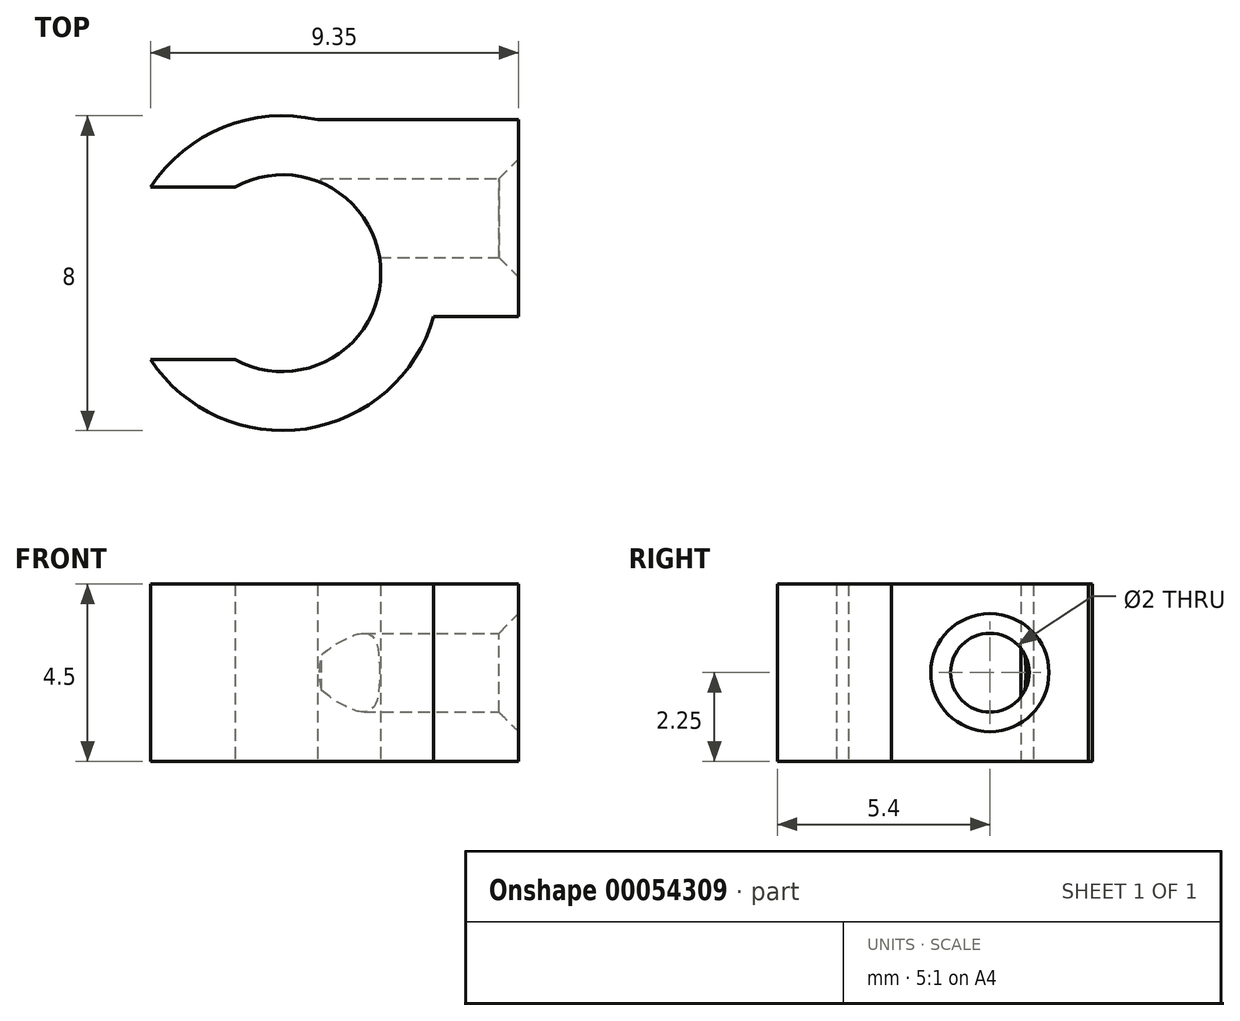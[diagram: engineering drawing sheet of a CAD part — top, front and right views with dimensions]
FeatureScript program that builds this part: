
annotation { "Feature Type Name" : "Feature", "Feature Type Description" : "" }
export const myFeature = defineFeature(function(context is Context, id is Id, definition is map)
    precondition{}
    {
        {
            var Q0;
            Q0=qCreatedBy(makeId("Top.planeOp"),FACE);
            var sketch = newSketch(context, id + "F0", { "sketchPlane" : qUnion([Q0])});
            skArc(sketch, "E0", {"start": v(-1.2, -2.2) * mm, "mid": v(2.5, 0) * mm, "end": v(-1.2, 2.2) * mm});
            skLineSegment(sketch, "E1", {"start": v(-1.2, 3.72) * mm, "end": v(-1.2, -3.37) * mm, "construction": true});
            skPoint(sketch, "E2", {"position": v(-1.2, 2.2) * mm});
            skPoint(sketch, "E3", {"position": v(-1.2, -2.2) * mm});
            skLineSegment(sketch, "E4", {"start": v(-4.97, 0) * mm, "end": v(6.07, 0) * mm, "construction": true});
            skLineSegment(sketch, "E5", {"start": v(6.07, 1.4) * mm, "end": v(1.32, 1.4) * mm, "construction": true});
            skLineSegment(sketch, "E6.bottom", {"start": v(6, -1.1) * mm, "end": v(3.85, -1.1) * mm});
            skLineSegment(sketch, "E6.top", {"start": v(6, 3.9) * mm, "end": v(0.89, 3.9) * mm});
            skLineSegment(sketch, "E6.left", {"start": v(6, -1.1) * mm, "end": v(6, 3.9) * mm});
            skArc(sketch, "E7.0", {"start": v(-3.35, -2.2) * mm, "mid": v(4, 0) * mm, "end": v(-3.35, 2.2) * mm});
            skLineSegment(sketch, "E8", {"start": v(-1.2, 2.2) * mm, "end": v(-3.35, 2.2) * mm});
            skLineSegment(sketch, "E9", {"start": v(-1.2, -2.2) * mm, "end": v(-3.35, -2.2) * mm});
            skSolve(sketch);
        }
        {
            var Q0;
            Q0=makeQuery(id+"F0.imprint","IMPRINT",FACE,{"disambiguationData":[TD([[makeQuery(id+"F0.imprint","IMPRINT",EDGE,{"derivedFrom":sQuery(id+"F0.wireOp",EDGE,"E0")}),-1.0]])]});
            var Q1;
            {var subQ0=sQuery(id+"F0.wireOp",EDGE,"E6.bottom");Q1=makeQuery(id+"F0.imprint","IMPRINT",FACE,{"disambiguationData":[TD([[makeQuery(id+"F0.imprint","IMPRINT",EDGE,{"derivedFrom":subQ0}),-1.0]])]});}
            extrude(context, id + "F1", {"entities" : qUnion([Q0, Q1]), "depth" : 4.5 * mm});
        }
        {
            var Q0;
            Q0=makeQuery(id+"F1.opExtrude","SWEPT_FACE",FACE,{"disambiguationData":[OSD([sQuery(id+"F0.wireOp",EDGE,"E6.left")])]});
            var sketch = newSketch(context, id + "F2", { "sketchPlane" : qUnion([Q0])});
            skLineSegment(sketch, "E10", {"start": v(1.4, 4.5) * mm, "end": v(1.4, 0) * mm, "construction": true});
            skLineSegment(sketch, "E11", {"start": v(7.13, 2.25) * mm, "end": v(-1.35, 2.25) * mm, "construction": true});
            skPoint(sketch, "E12", {"position": v(1.4, 2.25) * mm});
            skSolve(sketch);
        }
        {
            var Q0;
            Q0=sQuery(id+"F2.wireOp",VERTEX,"E12");
            var Q1;
            Q1=makeQuery(id+"F1.opExtrude","SWEPT_BODY",BODY,{"disambiguationData":[OSD([sQuery(id+"F0.wireOp",EDGE,"E0"),sQuery(id+"F0.wireOp",EDGE,"f4a43cd7-662f-42c6-86fa-e5735eea1d46.0"),sQuery(id+"F0.wireOp",EDGE,"64ae356d-9ca9-473f-8cb7-10ce9c5ed1fd"),sQuery(id+"F0.wireOp",EDGE,"50fe865a-2301-45af-9aee-2d7e59946f95"),sQuery(id+"F0.wireOp",EDGE,"E6.bottom"),sQuery(id+"F0.wireOp",EDGE,"E6.top"),sQuery(id+"F0.wireOp",EDGE,"E6.left"),sQuery(id+"F0.wireOp",EDGE,"13576935-0478-4a83-a7aa-48f961bede19.trimOffspring"),sQuery(id+"F0.wireOp",EDGE,"71bd9873-f9f2-4496-87d3-9368a0ced421.trimOffspring"),sQuery(id+"F0.wireOp",EDGE,"6accf4e7-3fb3-4be2-bdc0-6e3bf4705153.filletArc"),sQuery(id+"F0.wireOp",EDGE,"9a15b7b4-aaa0-4e66-8010-40df81dcd678.filletArc")])]});
            hole(context, id + "F3", {"style" : HoleStyle.C_SINK, "holeDiameter" : 2 * mm, "cSinkDiameter" : 3 * mm, "endStyle" : HoleEndStyle.BLIND, "holeDepth" : 5 * mm, "locations" : qUnion([Q0]), "scope" : qUnion([Q1]), "cSinkAngle" : 90 * degree});
        }
    });
